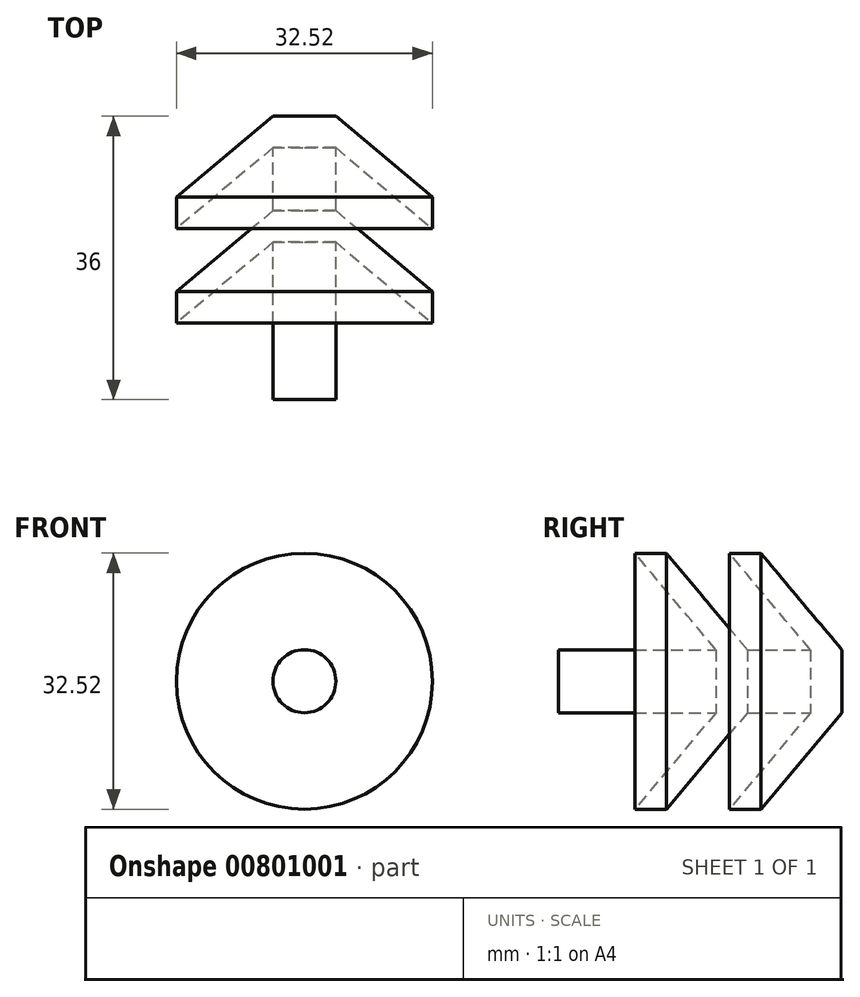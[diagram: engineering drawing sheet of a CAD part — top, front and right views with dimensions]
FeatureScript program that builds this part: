
annotation { "Feature Type Name" : "Feature", "Feature Type Description" : "" }
export const myFeature = defineFeature(function(context is Context, id is Id, definition is map)
    precondition{}
    {
        {
            var Q0;
            Q0=qCreatedBy(makeId("Top.planeOp"),FACE);
            var sketch = newSketch(context, id + "F0", { "sketchPlane" : qUnion([Q0])});
            skLineSegment(sketch, "E0", {"start": v(0, 0) * mm, "end": v(0, -36) * mm});
            skLineSegment(sketch, "E1", {"start": v(0, -36) * mm, "end": v(4, -36) * mm});
            skLineSegment(sketch, "E2", {"start": v(4, -36) * mm, "end": v(4, -16) * mm});
            skLineSegment(sketch, "E3", {"start": v(4, -16) * mm, "end": v(16.26, -26.28) * mm});
            skLineSegment(sketch, "E4", {"start": v(16.26, -26.28) * mm, "end": v(16.26, -22.28) * mm});
            skLineSegment(sketch, "E5", {"start": v(16.26, -22.28) * mm, "end": v(4, -12) * mm});
            skLineSegment(sketch, "E6", {"start": v(4, -12) * mm, "end": v(4, -4) * mm});
            skLineSegment(sketch, "E7", {"start": v(4, -4) * mm, "end": v(16.26, -14.28) * mm});
            skLineSegment(sketch, "E8", {"start": v(16.26, -14.28) * mm, "end": v(16.26, -10.28) * mm});
            skLineSegment(sketch, "E9", {"start": v(16.26, -10.28) * mm, "end": v(4, 0) * mm});
            skLineSegment(sketch, "E10", {"start": v(4, 0) * mm, "end": v(0, 0) * mm});
            skSolve(sketch);
        }
        {
            var Q0;
            Q0=makeQuery(id+"F0.imprint","IMPRINT",FACE,{"disambiguationData":[TD([[makeQuery(id+"F0.imprint","IMPRINT",EDGE,{"derivedFrom":sQuery(id+"F0.wireOp",EDGE,"E0")}),1.0]])]});
            var Q1;
            Q1=sQuery(id+"F0.wireOp",EDGE,"E0");
            revolve(context, id + "F1", {"surfaceOperationType" : NewSurfaceOperationType.NEW, "entities" : qUnion([Q0]), "axis" : qUnion([Q1]), "revolveType" : RevolveType.FULL});
        }
    });
